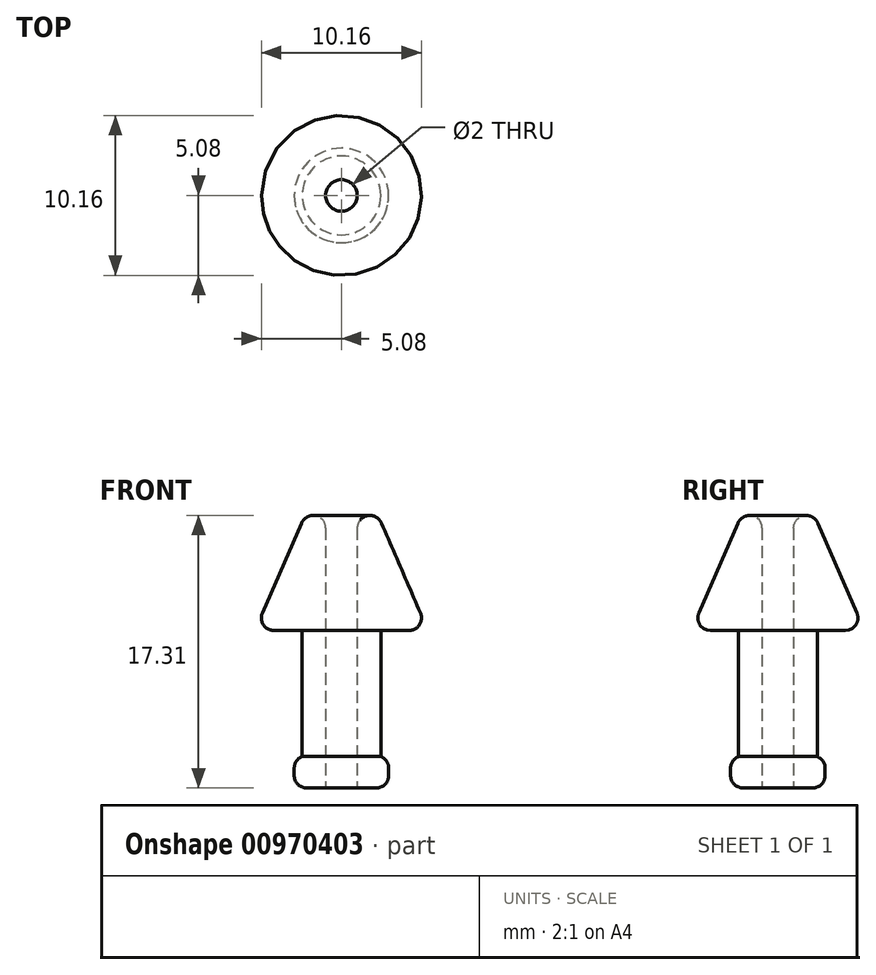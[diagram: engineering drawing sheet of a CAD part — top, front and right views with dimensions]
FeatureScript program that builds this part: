
annotation { "Feature Type Name" : "Feature", "Feature Type Description" : "" }
export const myFeature = defineFeature(function(context is Context, id is Id, definition is map)
    precondition{}
    {
        {
            var Q0;
            Q0=qCreatedBy(makeId("Front.planeOp"),FACE);
            var sketch = newSketch(context, id + "F0", { "sketchPlane" : qUnion([Q0])});
            skLineSegment(sketch, "E0", {"start": v(0, 0) * mm, "end": v(-2.5, 0) * mm, "construction": true});
            skLineSegment(sketch, "E1", {"start": v(0, 0) * mm, "end": v(-1, 0) * mm, "construction": true});
            skLineSegment(sketch, "E2", {"start": v(0, 0) * mm, "end": v(0, 26.78) * mm, "construction": true});
            skLineSegment(sketch, "E3", {"start": v(-1, 0) * mm, "end": v(-2.5, 0) * mm});
            skLineSegment(sketch, "E4", {"start": v(-2.5, 0) * mm, "end": v(-2.5, 10) * mm});
            skLineSegment(sketch, "E5", {"start": v(-2.5, 10) * mm, "end": v(-5.5, 10) * mm});
            skLineSegment(sketch, "E6", {"start": v(-5.5, 10) * mm, "end": v(-2.5, 16.92) * mm});
            skLineSegment(sketch, "E7", {"start": v(-2.5, 16.92) * mm, "end": v(-1, 18.7) * mm});
            skLineSegment(sketch, "E8", {"start": v(-1, 18.7) * mm, "end": v(-1, 0) * mm});
            skLineSegment(sketch, "E9", {"start": v(-2.5, 0) * mm, "end": v(-3, 0) * mm});
            skLineSegment(sketch, "E10", {"start": v(-3, 0) * mm, "end": v(-3, 2) * mm});
            skLineSegment(sketch, "E11", {"start": v(-3, 2) * mm, "end": v(-2.5, 2) * mm});
            skSolve(sketch);
        }
        {
            var Q0;
            Q0=makeQuery(id+"F0.imprint","IMPRINT",FACE,{"disambiguationData":[TD([[makeQuery(id+"F0.imprint","IMPRINT",EDGE,{"derivedFrom":sQuery(id+"F0.wireOp",EDGE,"E3")}),-1.0]])]});
            var Q1;
            {var subQ0=sQuery(id+"F0.wireOp",EDGE,"E9");Q1=makeQuery(id+"F0.imprint","IMPRINT",FACE,{"disambiguationData":[TD([[makeQuery(id+"F0.imprint","IMPRINT",EDGE,{"derivedFrom":subQ0}),-1.0]])]});}
            var Q2;
            Q2=sQuery(id+"F0.wireOp",EDGE,"E2");
            revolve(context, id + "F1", {"surfaceOperationType" : NewSurfaceOperationType.NEW, "entities" : qUnion([Q0, Q1]), "axis" : qUnion([Q2]), "revolveType" : RevolveType.FULL});
        }
        {
            var Q0;
            Q0=makeQuery(id+"F1.opRevolve","SWEPT_EDGE",EDGE,{"disambiguationData":[OSD([sQuery(id+"F0.wireOp",EDGE,"E6"),sQuery(id+"F0.wireOp",EDGE,"E7")])]});
            var Q1;
            Q1=makeQuery(id+"F1.opRevolve","SWEPT_EDGE",EDGE,{"disambiguationData":[OSD([sQuery(id+"F0.wireOp",EDGE,"E5"),sQuery(id+"F0.wireOp",EDGE,"E6")])]});
            var Q2;
            Q2=makeQuery(id+"F1.opRevolve","SWEPT_EDGE",EDGE,{"disambiguationData":[OSD([sQuery(id+"F0.wireOp",EDGE,"E7"),sQuery(id+"F0.wireOp",EDGE,"E8")])]});
            var Q3;
            Q3=makeQuery(id+"F1.opRevolve","SWEPT_EDGE",EDGE,{"disambiguationData":[OSD([sQuery(id+"F0.wireOp",EDGE,"E10"),sQuery(id+"F0.wireOp",EDGE,"E11")])]});
            var Q4;
            Q4=makeQuery(id+"F1.opRevolve","SWEPT_EDGE",EDGE,{"disambiguationData":[OSD([sQuery(id+"F0.wireOp",EDGE,"E9"),sQuery(id+"F0.wireOp",EDGE,"E10")])]});
            fillet(context, id + "F2", {"entities" : qUnion([Q0, Q1, Q2, Q3, Q4]), "radius" : .8 * mm, "tangentPropagation" : true, "allowEdgeOverflow" : false});
        }
    });
